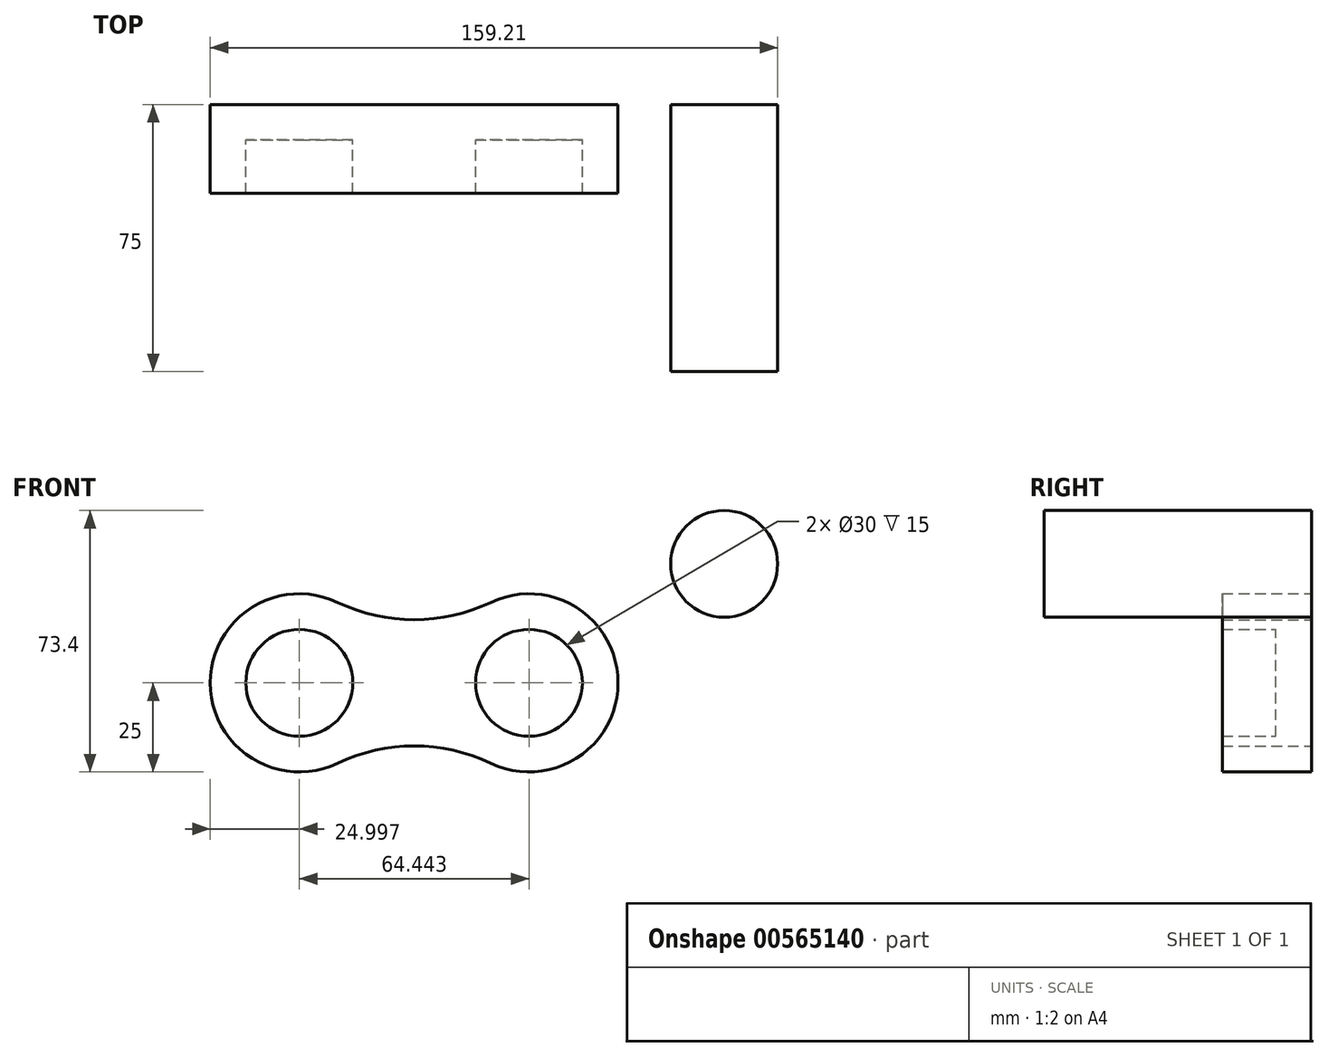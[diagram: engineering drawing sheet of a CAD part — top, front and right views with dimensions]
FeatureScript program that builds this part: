
annotation { "Feature Type Name" : "Feature", "Feature Type Description" : "" }
export const myFeature = defineFeature(function(context is Context, id is Id, definition is map)
    precondition{}
    {
        {
            var Q0;
            Q0=qCreatedBy(makeId("Front.planeOp"),FACE);
            var sketch = newSketch(context, id + "F0", { "sketchPlane" : qUnion([Q0])});
            skCircle(sketch, "E0", {"center": v(0, 0) * mm, "radius": 25 * mm});
            skCircle(sketch, "E1", {"center": v(-64.44, 0) * mm, "radius": 25 * mm});
            skArc(sketch, "E2", {"start": v(-53.7, 22.58) * mm, "mid": v(-32.22, 17.73) * mm, "end": v(-10.74, 22.58) * mm});
            skArc(sketch, "E3.MirrorCS", {"start": v(-53.7, -22.58) * mm, "mid": v(-32.22, -17.73) * mm, "end": v(-10.74, -22.58) * mm});
            skCircle(sketch, "E4", {"center": v(-64.44, 0) * mm, "radius": 15 * mm});
            skCircle(sketch, "E5", {"center": v(0, 0) * mm, "radius": 15 * mm});
            skSolve(sketch);
        }
        {
            var Q0;
            Q0=makeQuery(id+"F0.imprint","IMPRINT",FACE,{"disambiguationData":[TD([[makeQuery(id+"F0.imprint","IMPRINT",EDGE,{"derivedFrom":sQuery(id+"F0.wireOp",EDGE,"E4")}),-1.0]])]});
            var Q1;
            {var subQ0=sQuery(id+"F0.wireOp",EDGE,"E2");Q1=makeQuery(id+"F0.imprint","IMPRINT",FACE,{"disambiguationData":[TD([[makeQuery(id+"F0.imprint","IMPRINT",EDGE,{"derivedFrom":subQ0}),-1.0]])]});}
            var Q2;
            Q2=makeQuery(id+"F0.imprint","IMPRINT",FACE,{"disambiguationData":[TD([[makeQuery(id+"F0.imprint","IMPRINT",EDGE,{"derivedFrom":sQuery(id+"F0.wireOp",EDGE,"E5")}),-1.0]])]});
            extrude(context, id + "F1", {"entities" : qUnion([Q0, Q1, Q2]), "depth" : 25 * mm, "offsetDistance" : 25 * mm});
        }
        {
            var Q0;
            Q0=makeQuery(id+"F0.imprint","IMPRINT",FACE,{"disambiguationData":[TD([[makeQuery(id+"F0.imprint","IMPRINT",EDGE,{"derivedFrom":sQuery(id+"F0.wireOp",EDGE,"E5")}),1.0]])]});
            var Q1;
            Q1=makeQuery(id+"F0.imprint","IMPRINT",FACE,{"disambiguationData":[TD([[makeQuery(id+"F0.imprint","IMPRINT",EDGE,{"derivedFrom":sQuery(id+"F0.wireOp",EDGE,"E4")}),1.0]])]});
            extrude(context, id + "F2", {"entities" : qUnion([Q0, Q1]), "operationType" : NewBodyOperationType.ADD, "depth" : 10 * mm, "offsetDistance" : 25 * mm});
        }
        {
            var Q0;
            Q0=qCreatedBy(makeId("Front.planeOp"),FACE);
            var sketch = newSketch(context, id + "F3", { "sketchPlane" : qUnion([Q0])});
            skCircle(sketch, "E6", {"center": v(54.77, 33.4) * mm, "radius": 15 * mm});
            skSolve(sketch);
        }
        {
            var Q0;
            Q0 = qSketchRegion(id + "F3", true);
            extrude(context, id + "F4", {"entities" : qUnion([Q0]), "depth" : 75 * mm, "offsetDistance" : 25 * mm});
        }
    });
